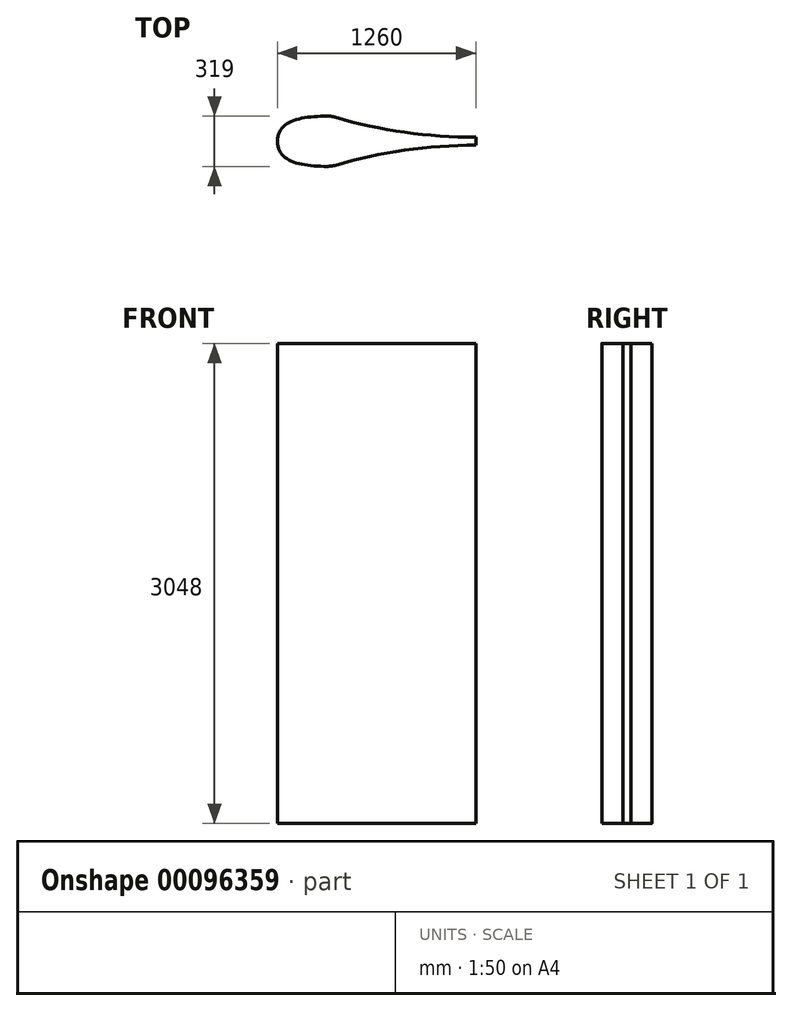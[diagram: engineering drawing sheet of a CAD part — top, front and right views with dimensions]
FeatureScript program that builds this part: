
annotation { "Feature Type Name" : "Feature", "Feature Type Description" : "" }
export const myFeature = defineFeature(function(context is Context, id is Id, definition is map)
    precondition{}
    {
        {
            var Q0;
            Q0=qCreatedBy(makeId("Top.planeOp"),FACE);
            var sketch = newSketch(context, id + "F0", { "sketchPlane" : qUnion([Q0])});
            skLineSegment(sketch, "E0", {"start": v(0, 0) * mm, "end": v(1450, 0) * mm, "construction": true});
            skLineSegment(sketch, "E1.top", {"start": v(0, 159.5) * mm, "end": v(1450, 159.5) * mm, "construction": true});
            skLineSegment(sketch, "E1.left", {"start": v(0, 0) * mm, "end": v(0, 159.5) * mm, "construction": true});
            skLineSegment(sketch, "E1.right", {"start": v(1450, 0) * mm, "end": v(1450, 159.5) * mm, "construction": true});
            skLineSegment(sketch, "E2", {"start": v(319, -455.75) * mm, "end": v(319, 399.96) * mm, "construction": true});
            skLineSegment(sketch, "E3", {"start": v(0, 0) * mm, "end": v(0, 0) * mm});
            skCircle(sketch, "E4", {"center": v(319, 0) * mm, "radius": 319 * mm, "construction": true});
            skFitSpline(sketch, "E5", {"points": [v(0, 0) * mm, v(319, 159.5) * mm], "startDerivative": vector(0, 394.6) * mm, "endDerivative": vector(517.63, 0) * mm});
            skLineSegment(sketch, "E6", {"start": v(1260, -87.61) * mm, "end": v(1260, 215.35) * mm, "construction": true});
            skLineSegment(sketch, "E7", {"start": v(1260, 0) * mm, "end": v(1260, 25) * mm});
            skLineSegment(sketch, "E8", {"start": v(319, 159.5) * mm, "end": v(1260, 25) * mm, "construction": true});
            skArc(sketch, "E9", {"start": v(319, 159.5) * mm, "mid": v(341.57, 157.9) * mm, "end": v(363.68, 153.11) * mm});
            skArc(sketch, "E10", {"start": v(363.68, 153.11) * mm, "mid": v(807.29, 57.2) * mm, "end": v(1260, 25) * mm});
            skFitSpline(sketch, "E11.MirrorCS", {"points": [v(0, 0) * mm, v(319, -159.5) * mm], "startDerivative": vector(0, -394.6) * mm, "endDerivative": vector(517.63, 0) * mm});
            skArc(sketch, "E12.MirrorCS", {"start": v(319, -159.5) * mm, "mid": v(341.57, -157.9) * mm, "end": v(363.68, -153.11) * mm});
            skArc(sketch, "E13.MirrorCS", {"start": v(363.68, -153.11) * mm, "mid": v(807.29, -57.2) * mm, "end": v(1260, -25) * mm});
            skLineSegment(sketch, "E14.MirrorCS", {"start": v(1260, 0) * mm, "end": v(1260, -25) * mm});
            skSolve(sketch);
        }
        {
            var Q0;
            Q0 = qSketchRegion(id + "F0", true);
            extrude(context, id + "F1", {"entities" : qUnion([Q0]), "depth" : 3048 * mm});
        }
    });
